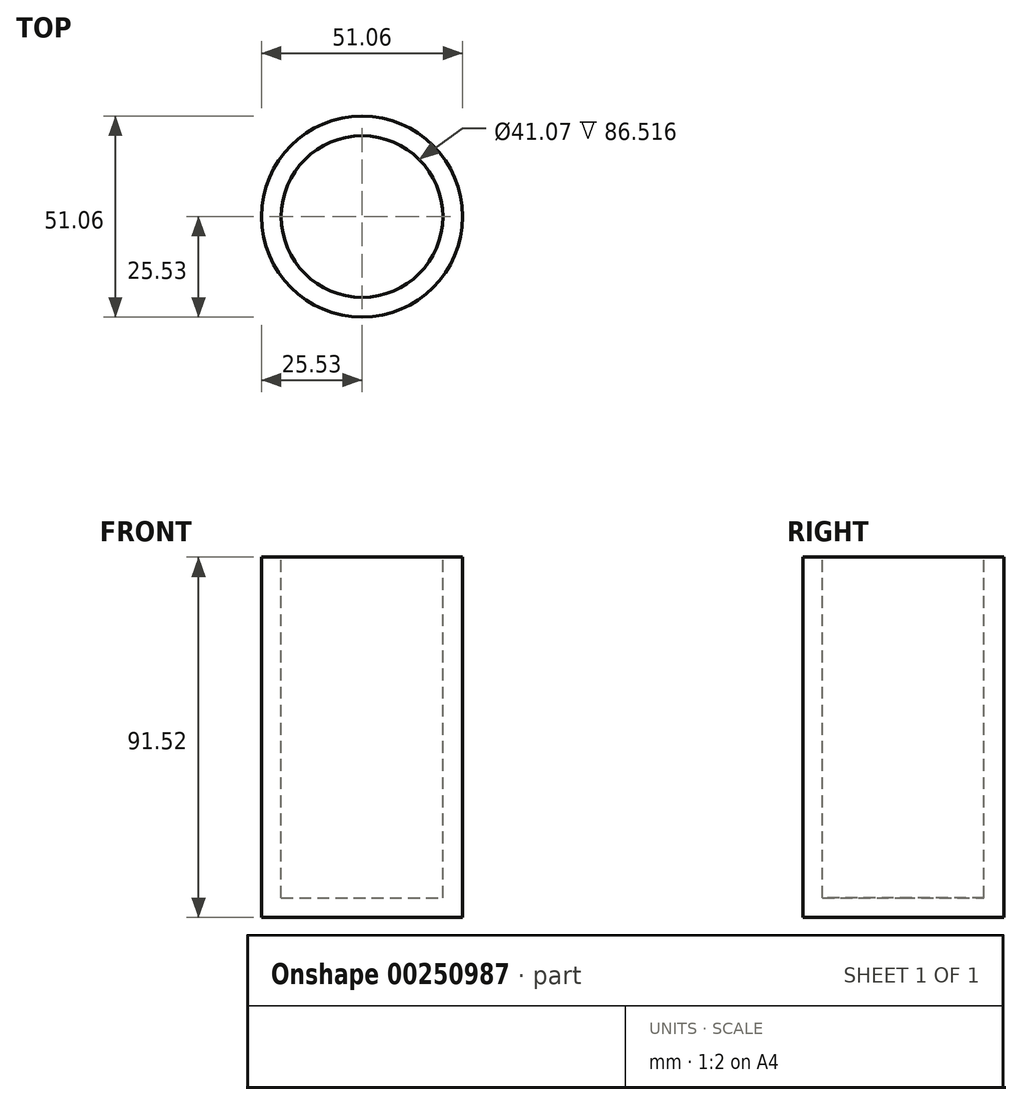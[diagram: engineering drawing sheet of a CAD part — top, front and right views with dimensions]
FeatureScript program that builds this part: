
annotation { "Feature Type Name" : "Feature", "Feature Type Description" : "" }
export const myFeature = defineFeature(function(context is Context, id is Id, definition is map)
    precondition{}
    {
        {
            var Q0;
            Q0=qCreatedBy(makeId("Front.planeOp"),FACE);
            var sketch = newSketch(context, id + "F0", { "sketchPlane" : qUnion([Q0])});
            skLineSegment(sketch, "E0.bottom", {"start": v(-25.53, 45.76) * mm, "end": v(25.53, 45.76) * mm});
            skLineSegment(sketch, "E0.top", {"start": v(-25.53, -45.76) * mm, "end": v(25.53, -45.76) * mm});
            skLineSegment(sketch, "E0.left", {"start": v(-25.53, 45.76) * mm, "end": v(-25.53, -45.76) * mm});
            skLineSegment(sketch, "E0.right", {"start": v(25.53, 45.76) * mm, "end": v(25.53, -45.76) * mm});
            skPoint(sketch, "E0.middle", {"position": v(0, 0) * mm});
            skLineSegment(sketch, "E1", {"start": v(0, 45.76) * mm, "end": v(0, -45.76) * mm});
            skSolve(sketch);
        }
        {
            var Q0;
            {var subQ0=sQuery(id+"F0.wireOp",EDGE,"E0.left");Q0=makeQuery(id+"F0.imprint","IMPRINT",FACE,{"disambiguationData":[TD([[makeQuery(id+"F0.imprint","IMPRINT",EDGE,{"derivedFrom":subQ0}),1.0]])]});}
            var Q1;
            Q1=sQuery(id+"F0.wireOp",EDGE,"E1");
            revolve(context, id + "F1", {"entities" : qUnion([Q0]), "axis" : qUnion([Q1]), "revolveType" : RevolveType.FULL});
        }
        {
            var Q0;
            Q0=makeQuery(id+"F1.opRevolve","SWEPT_FACE",FACE,{"disambiguationData":[OSD([sQuery(id+"F0.wireOp",EDGE,"E0.bottom")])]});
            shell(context, id + "F2", {"entities" : qUnion([Q0]), "thickness" : 5 * mm});
        }
    });
